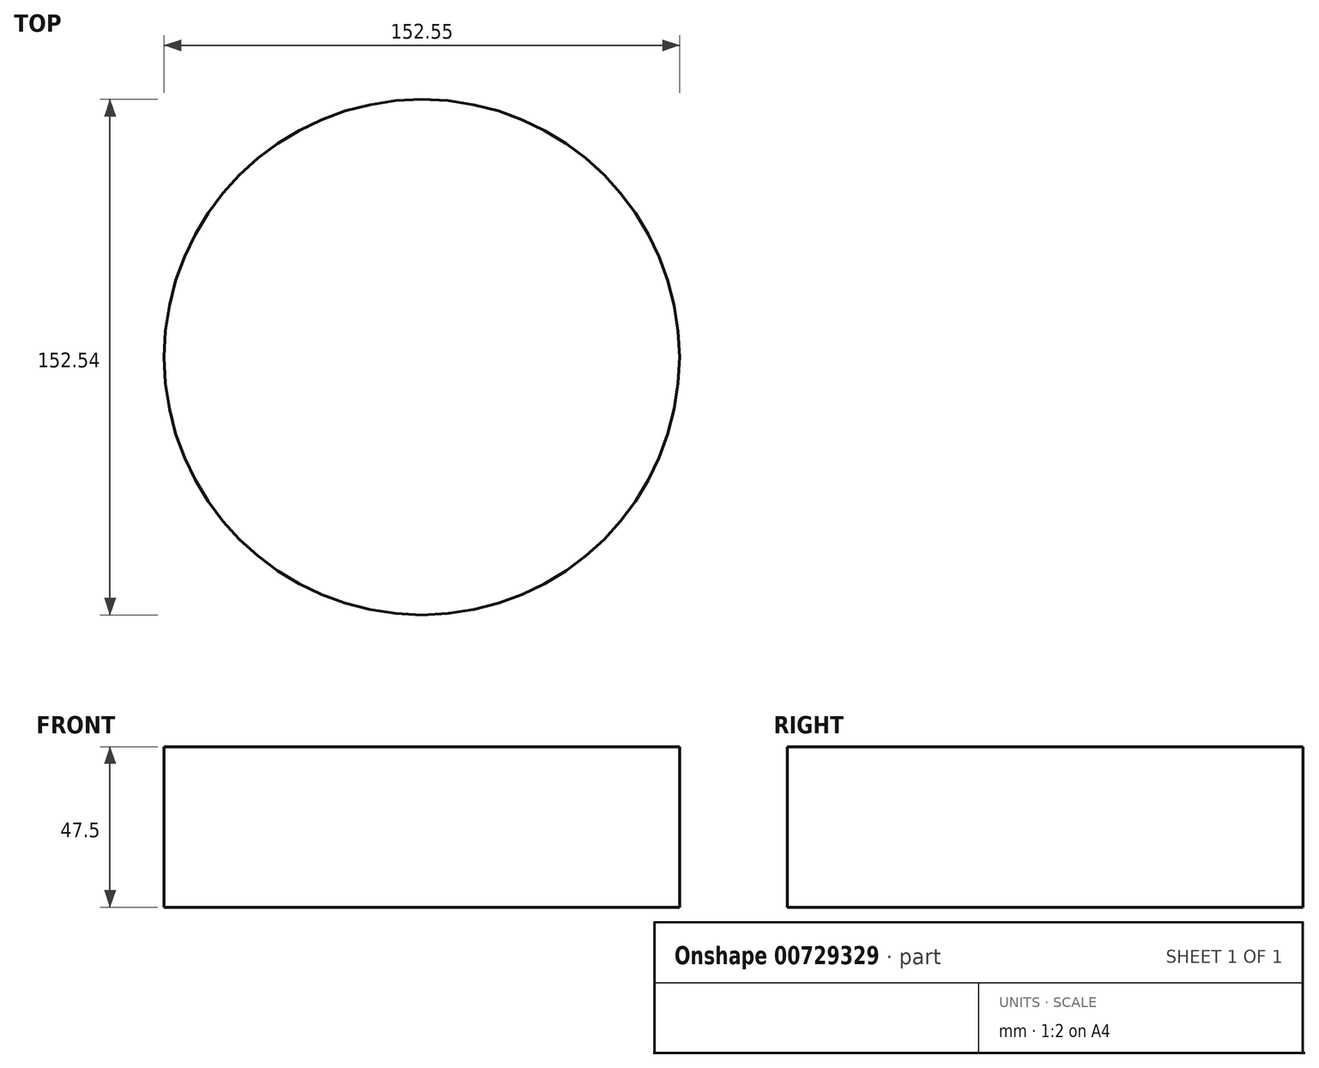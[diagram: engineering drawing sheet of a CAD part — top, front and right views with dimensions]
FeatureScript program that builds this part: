
annotation { "Feature Type Name" : "Feature", "Feature Type Description" : "" }
export const myFeature = defineFeature(function(context is Context, id is Id, definition is map)
    precondition{}
    {
        {
            var Q0;
            Q0=qCreatedBy(makeId("Top.planeOp"),FACE);
            var sketch = newSketch(context, id + "F0", { "sketchPlane" : qUnion([Q0])});
            skCircle(sketch, "E0", {"center": v(-152.9, 0) * mm, "radius": 76.27 * mm});
            skSolve(sketch);
        }
        {
            var Q0;
            Q0=makeQuery(id+"F0.imprint","IMPRINT",FACE,{"disambiguationData":[TD([[makeQuery(id+"F0.imprint","IMPRINT",EDGE,{"derivedFrom":sQuery(id+"F0.wireOp",EDGE,"E0")}),1.0]])]});
            extrude(context, id + "F1", {"entities" : qUnion([Q0]), "depth" : 47.5 * mm, "offsetDistance" : 25.4 * mm});
        }
    });
